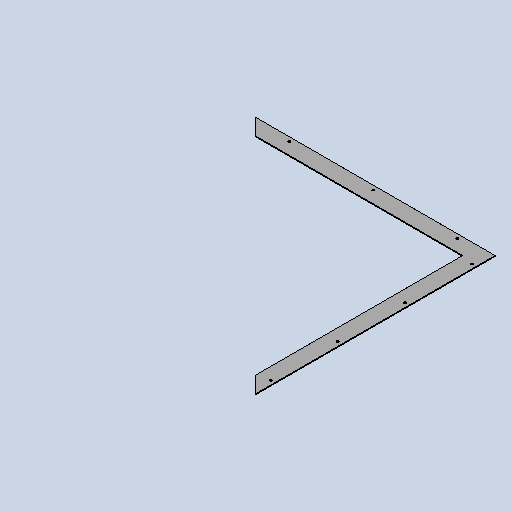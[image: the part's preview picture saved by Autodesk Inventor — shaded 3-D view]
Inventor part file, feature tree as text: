
AUTODESK INVENTOR PART (.ipt)
format: ipt  version: 2025.3 (Build 293356030, 356C)  size: 194,560 bytes
history: native  units: mm
features: other x4, sketch x2, sheet_metal_op x1, projected_geometry x1
ambient origin geometry x8: Origin, YZ Plane, XZ Plane, XY Plane, X Axis, Y Axis, Z Axis, Center Point
bodies: Solid1 (feature_tree)
feature tree (8):
  sheet_metal_op  "Face1"
  other  "Corner Chamfer1"
  sketch  "Sketch1"  dims[d1=570.0mm]
  other  "Plate1"
  sketch  "Sketch2"  dims[d2=493.0mm d3=2.0mm d4=1.0mm d5=6.0mm d6=45.0deg d7=5.5mm d8=10.0mm d9=10.0mm d10=80.0mm d11=80.0mm d12=240.0mm d13=240.0mm d14=200.0mm d15=200.0mm d16=2.0mm d17=0.0mm]
  projected_geometry  "Projected Loop1"
  other  "Cut1"
  other  "Definition1"
